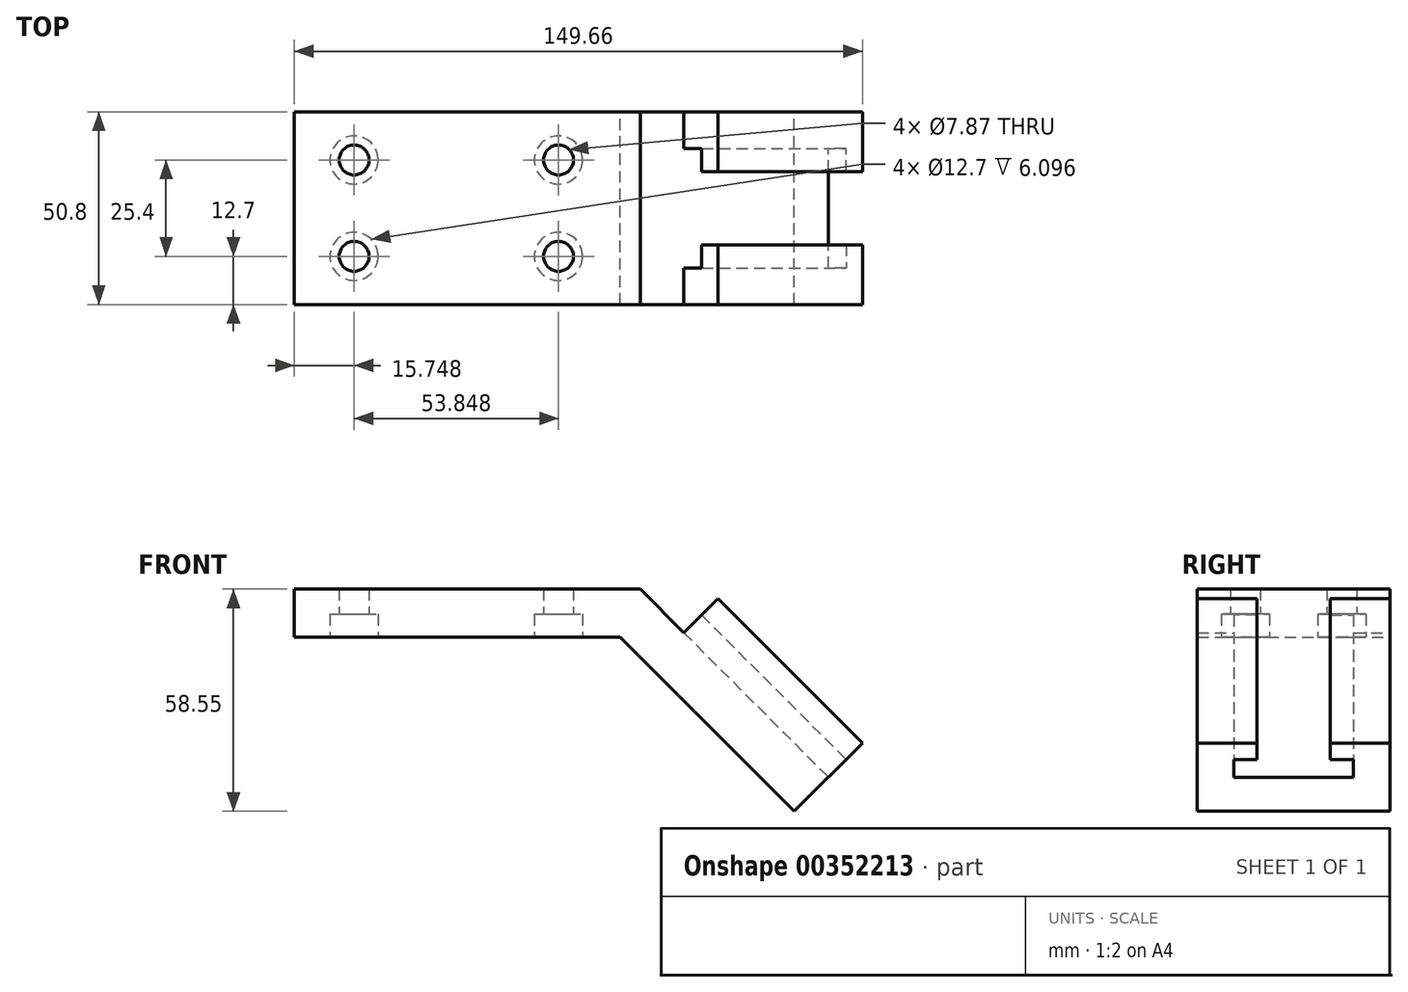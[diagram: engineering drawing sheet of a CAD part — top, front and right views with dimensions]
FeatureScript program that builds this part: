
annotation { "Feature Type Name" : "Feature", "Feature Type Description" : "" }
export const myFeature = defineFeature(function(context is Context, id is Id, definition is map)
    precondition{}
    {
        {
            var Q0;
            Q0=qCreatedBy(makeId("Front.planeOp"),FACE);
            var sketch = newSketch(context, id + "F0", { "sketchPlane" : qUnion([Q0])});
            skLineSegment(sketch, "E0", {"start": v(0, 0) * mm, "end": v(0, 12.7) * mm});
            skLineSegment(sketch, "E1", {"start": v(102.6, 1.2) * mm, "end": v(111.59, 10.19) * mm});
            skLineSegment(sketch, "E2", {"start": v(111.59, 10.19) * mm, "end": v(149.66, -27.9) * mm});
            skLineSegment(sketch, "E3", {"start": v(149.66, -27.9) * mm, "end": v(131.7, -45.85) * mm});
            skLineSegment(sketch, "E4", {"start": v(85.85, 0) * mm, "end": v(0, 0) * mm});
            skLineSegment(sketch, "E5", {"start": v(91.11, 12.7) * mm, "end": v(102.6, 1.2) * mm});
            skLineSegment(sketch, "E6", {"start": v(0, 12.7) * mm, "end": v(91.11, 12.7) * mm});
            skLineSegment(sketch, "E7", {"start": v(85.85, 0) * mm, "end": v(131.7, -45.85) * mm});
            skSolve(sketch);
        }
        {
            var Q0;
            Q0 = qSketchRegion(id + "F0", true);
            extrude(context, id + "F1", {"entities" : qUnion([Q0]), "depth" : 50.8 * mm});
        }
        {
            var Q0;
            Q0=makeQuery(id+"F1.opExtrude","SWEPT_FACE",FACE,{"disambiguationData":[OSD([sQuery(id+"F0.wireOp",EDGE,"E3")])]});
            var sketch = newSketch(context, id + "F2", { "sketchPlane" : qUnion([Q0])});
            skLineSegment(sketch, "E8", {"start": v(-25.4, 90.03) * mm, "end": v(-25.4, 57.37) * mm});
            skPoint(sketch, "E8.startSnap0", {"position": v(-25.4, 86.1) * mm});
            skLineSegment(sketch, "E9", {"start": v(-25.4, 86.1) * mm, "end": v(-35.05, 86.1) * mm});
            skLineSegment(sketch, "E10", {"start": v(-35.05, 86.1) * mm, "end": v(-35.05, 80.01) * mm});
            skLineSegment(sketch, "E11", {"start": v(-35.05, 80.01) * mm, "end": v(-41.15, 80.01) * mm});
            skLineSegment(sketch, "E12", {"start": v(-41.15, 80.01) * mm, "end": v(-41.15, 73.4) * mm});
            skLineSegment(sketch, "E13", {"start": v(-41.15, 73.4) * mm, "end": v(-25.4, 73.4) * mm});
            skPoint(sketch, "E13.endSnap0", {"position": v(-25.4, 73.7) * mm});
            skLineSegment(sketch, "E14", {"start": v(-25.4, 73.4) * mm, "end": v(-25.4, 86.1) * mm});
            skLineSegment(sketch, "E15.MirrorCS", {"start": v(-25.4, 86.1) * mm, "end": v(-15.75, 86.1) * mm});
            skLineSegment(sketch, "E16.MirrorCS", {"start": v(-15.75, 86.1) * mm, "end": v(-15.75, 80.01) * mm});
            skLineSegment(sketch, "E17.MirrorCS", {"start": v(-15.75, 80.01) * mm, "end": v(-9.65, 80.01) * mm});
            skLineSegment(sketch, "E18.MirrorCS", {"start": v(-9.65, 80.01) * mm, "end": v(-9.65, 73.4) * mm});
            skLineSegment(sketch, "E19.MirrorCS", {"start": v(-9.65, 73.4) * mm, "end": v(-25.4, 73.4) * mm});
            skSolve(sketch);
        }
        {
            var Q0;
            Q0 = qSketchRegion(id + "F2", true);
            extrude(context, id + "F3", {"entities" : qUnion([Q0]), "operationType" : NewBodyOperationType.REMOVE, "oppositeDirection" : true, "depth" : 53.85 * mm});
        }
        {
            var Q0;
            {var subQ1=sQuery(id+"F0.wireOp",EDGE,"E2");Q0=makeQuery(id+"F3.boolean.opBoolean","SPLIT",FACE,{"disambiguationData":[TD([makeQuery(id+"F3.opExtrude","SWEPT_FACE",FACE,{"disambiguationData":[OSD([sQuery(id+"F2.wireOp",EDGE,"E10")])]})])],"derivedFrom":makeQuery(id+"F1.opExtrude","SWEPT_FACE",FACE,{"disambiguationData":[OSD([subQ1])]})});}
            var sketch = newSketch(context, id + "F4", { "sketchPlane" : qUnion([Q0])});
            skLineSegment(sketch, "E20", {"start": v(71.7, 0) * mm, "end": v(71.7, -50.8) * mm, "construction": true});
            skArc(sketch, "E21", {"start": v(71.7, -79.25) * mm, "mid": v(125.55, -25.3) * mm, "end": v(71.52, 28.45) * mm});
            skPoint(sketch, "E21.startSnap0", {"position": v(71.7, -25.4) * mm});
            skLineSegment(sketch, "E22", {"start": v(71.7, -79.25) * mm, "end": v(71.52, 28.45) * mm});
            skLineSegment(sketch, "E23", {"start": v(125.55, 0) * mm, "end": v(125.55, -25.4) * mm});
            skLineSegment(sketch, "E24", {"start": v(125.55, 0) * mm, "end": v(119.18, 0) * mm});
            skLineSegment(sketch, "E25", {"start": v(125.55, -25.4) * mm, "end": v(192.2, -25.4) * mm, "construction": true});
            skPoint(sketch, "E25.endSnap0", {"position": v(71.6, -25.4) * mm});
            skLineSegment(sketch, "E26.MirrorCS", {"start": v(125.55, -50.8) * mm, "end": v(125.55, -25.4) * mm});
            skLineSegment(sketch, "E27.MirrorCS", {"start": v(125.55, -50.8) * mm, "end": v(119.18, -50.8) * mm});
            skSolve(sketch);
        }
        {
            var Q0;
            {var subQ0=sQuery(id+"F4.wireOp",EDGE,"E27.MirrorCS");Q0=makeQuery(id+"F4.imprint","IMPRINT",FACE,{"disambiguationData":[TD([[makeQuery(id+"F4.imprint","IMPRINT",EDGE,{"derivedFrom":subQ0}),1.0]])]});}
            var Q1;
            {var subQ0=sQuery(id+"F4.wireOp",EDGE,"E26.MirrorCS");var subQ1=sQuery(id+"F4.wireOp",EDGE,"E21");var subQ2=makeQuery(id+"F4.imprint","INTERSECT",VERTEX,{"derivedFrom":[subQ1,subQ0]});Q1=makeQuery(id+"F4.imprint","IMPRINT",FACE,{"disambiguationData":[TD([[makeQuery(id+"F4.imprint","IMPRINT",EDGE,{"disambiguationData":[TD([[subQ2,1.0]])],"derivedFrom":subQ1}),-1.0]])]});}
            var Q2;
            {var subQ0=sQuery(id+"F4.wireOp",EDGE,"E23");Q2=makeQuery(id+"F4.imprint","IMPRINT",FACE,{"disambiguationData":[TD([[makeQuery(id+"F4.imprint","IMPRINT",EDGE,{"derivedFrom":subQ0}),-1.0]])]});}
            extrude(context, id + "F5", {"entities" : qUnion([Q0, Q1, Q2]), "operationType" : NewBodyOperationType.REMOVE, "endBound" : BoundingType.THROUGH_ALL, "oppositeDirection" : true, "depth" : 25.4 * mm});
        }
        {
            var Q0;
            Q0=makeQuery(id+"F1.opExtrude","SWEPT_FACE",FACE,{"disambiguationData":[OSD([sQuery(id+"F0.wireOp",EDGE,"E4")])]});
            var sketch = newSketch(context, id + "F6", { "sketchPlane" : qUnion([Q0])});
            skPoint(sketch, "E28", {"position": v(15.75, 12.7) * mm});
            skPoint(sketch, "E29", {"position": v(69.6, 12.7) * mm});
            skPoint(sketch, "E30", {"position": v(69.6, 38.1) * mm});
            skPoint(sketch, "E31", {"position": v(15.75, 38.1) * mm});
            skSolve(sketch);
        }
        {
            var Q0;
            Q0=sQuery(id+"F6.wireOp",VERTEX,"E28");
            var Q1;
            Q1=sQuery(id+"F6.wireOp",VERTEX,"E31");
            var Q2;
            Q2=sQuery(id+"F6.wireOp",VERTEX,"E29");
            var Q3;
            Q3=sQuery(id+"F6.wireOp",VERTEX,"E30");
            var Q4;
            Q4=makeQuery(id+"F1.opExtrude","SWEPT_BODY",BODY,{"disambiguationData":[OSD([sQuery(id+"F0.wireOp",EDGE,"E0"),sQuery(id+"F0.wireOp",EDGE,"E1"),sQuery(id+"F0.wireOp",EDGE,"E2"),sQuery(id+"F0.wireOp",EDGE,"E3"),sQuery(id+"F0.wireOp",EDGE,"E4"),sQuery(id+"F0.wireOp",EDGE,"E5"),sQuery(id+"F0.wireOp",EDGE,"E6"),sQuery(id+"F0.wireOp",EDGE,"E7")])]});
            hole(context, id + "F7", {"style" : HoleStyle.C_BORE, "endStyle" : HoleEndStyle.THROUGH, "holeDiameter" : 7.87 * mm, "cBoreDiameter" : 12.7 * mm, "cBoreDepth" : 6.1 * mm, "isTappedThrough" : true, "tappedDepth" : 12.7 * mm, "tapClearance" : 3, "locations" : qUnion([Q0, Q1, Q2, Q3]), "scope" : qUnion([Q4])});
        }
    });
